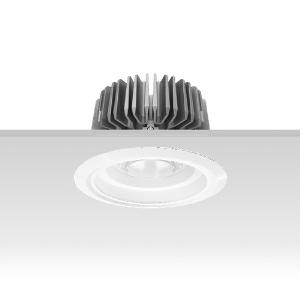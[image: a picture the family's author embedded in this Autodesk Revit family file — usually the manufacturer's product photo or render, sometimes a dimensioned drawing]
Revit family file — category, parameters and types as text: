
# Revit family: 3f_filippi_-_3f_reno_bianco_ampio_3f_filippi_-_30353_a01023_-_3f_reno_150_wh_3000-930_wide___vt_wh_1a36
name_source: partatom
category: Lighting Fixtures
units: mm (PartAtom-declared; Revit-internal decimal feet)

## family parameters
Cut with Voids When Loaded = No
Host = Face
Light Source = No
Part Type = Normal
Room Calculation Point = No
Round Connector Dimension = Use Diameter
Shared = No

## types (1)
- 3F Filippi - 3F Reno Bianco Ampio (1 x LED, 2656 lm, 37 W, 3000 K)
    Apparent Load = 37 VA
    Approval mark = CE
    CIE Flux Codes = 74 93 99 100 100
    Color Rendering = 90
    Color Temperature = 3000 K
    Control Gear = Electronic ballast
    Default Elevation = 1800 mm
    Description = ILLUMINOTECHNICAL
Luminous efficiency 100% (DLOR 100%, ULOR 0%).
Initial luminous flux of the luminaire 2656 lm.
Direct symmetric wide distribution.
Installation Interdistance Transv.D = 1.54 x hu - Long.D = 1.54 x hu.
Tabular UGR (CIE 117 - 4H-8H; S=0.25H; 70/50/20): RUG 24.4 - 24.2.
Beam angle: 74° - 73°.
Luminous efficacy 72 lm/W.
Lifetime (L90/B10): 30000 h. (tq+25°C)
Lifetime (L85/B10): 50000 h. (tq+25°C)
Lifetime (L70/B10): 80000 h. (tq+25°C)
Sudden decreased luminous flux after 50000 hours: 0% (C0).
Photobiological safety in compliance with IEC/TR 62778: RG0 risk exempt, (IEC 62471).
In compliance with IEC/EN 62722-2-1 - IEC/EN 62717 standards.

SOURCE
Compact LED module 3000/930.
Energy efficiency class (UE 2019/2020 - UE 2019/2015): E.
CIE 13.3 Colour rendering index: CRI >90 (R9 >50%).
IES TM-30 Fidelity Index: Rf = 92 Rg = 101.
CCT nominal colour temperature 3000 K.
Colour initial tolerance (MacAdam): SDCM 3.
Zhaga Book 3 compliant.

MECHANICAL
Passive heat dissipator in die-casting aluminium, oversized, for optimum thermal management of the LED module.
Parabolic element with graduated/concentric rings in white polycarbonate.
Transparent external lens with glossy and satin differentiated surfaces, with a cooling and anti-insect system in methacrylate (PMMA).
Fastening spring clips in stainless steel.
Dimensions: diameter 176 mm, height 111 mm. Weight 1.455 kg.
IP44 protection degree for exposed part, IP20 for recessed part.
Mechanical strength to impacts IK06 (1 joule).
Glow-wire test resistance 650°C.

ELECTRICAL
Wiring on a separate unit.
Halogen Free electronic wiring 230V-50/60Hz, power factor 0.95, THD <25%, constant output current, SELV, class II, 1 driver.
Power of the luminaire 37 W.
ENEC - CE.
SAFE FLICKER: PstLM=<1 and SVM=<0.4 (IEC TR 61547-1 and IEC TR 63158), to ensure a more comfortable and safe light.
Luminaire compliant with EN 60598-2-22 for power supply from a centralised emergency system CPSS (Central Power Supply System), not incorporated in the luminaire - high risk areas excluded. The default power and flux are 100% in AC and 100% in DC.
Ambient temperature from 0°C to +25°C.
Temperature class T6 max 85°C.
Relative humidity UR: <85%.

INSTALLATION
Pull-up recessed fitting.
False ceiling carving: 150 mm.
All accessories dedicated to this product are available on the Catalog and on our website www.3F-Filippi.com.

ACCESSORIES
A01023 - VT transparent glass, tempered, not flammable, locked and in line with the trim, in white polycarbonate.

APPLICATIONS
Environments: architectural, commercial, exhibition areas, transit areas, corridors, shops, display windows, service areas.
In false ceilings with narrow voids.

WARNING
Luminaire designed for disposal/recycling at end-of-life.
Replaceable (LED only) light source by a professional. Replaceable control gear by a professional.
    Height = 0 mm  [stored 0 ft]
    Lamp = 1 x LED
    Lamp Light Flux = 2656 lm
    Lamp Power = 37 W
    Lamp count = 1
    Length = 176 mm
    Lifetime = 50000 h
    Luminous efficacy = 72 lm/W
    Manufacturer = 3F Filippi
    ModVariant = No
    Model = 3F Filippi - 30353+A01023 - 3F Reno 150 WH 3000-930 WIDE + VT WH
    Mounting Place = Ceiling
    Mounting Type = Recessed
    Number of Poles = 1
    OnlyDefault = Yes
    Power Factor = 1
    Product Name = 3F Filippi - 3F Reno Bianco Ampio
    Product group = recessed luminaire
    ProductGroupID = 4
    Protection Class = Protection class II
    Protection Degree = IP 20
    RLX_Detail_Level = 1
    RLX_Emergency_Light_Flux = 0 lm
    RLX_Emergency_Type = 0
    RLX_Emergency_Type_DB = No
    RlxData = <blob elided: 85701 chars, md5=58da81eb>
    Socket = socket
    Standby Power = 0 W
    System Light Flux = 2656 lm
    System Power = 37 W
    Type Comments = Product without accessories
    Type Image = 3ffilippi_3f_reno_150_wh_d150__a01023.jpg
    URL = http://relux.com
    VarID = ---
    Voltage = 0 V
    Weight = 0.00 kg
    Width = 0 mm  [stored 0 ft]

note: [stored X ft] marks values corroborated as IEEE doubles in the binary element streams (Revit-internal decimal feet)

## geometry (parser evidence)
native form markers: Blend x4, Sweep x11
no freeform markers — native parametric forms only
